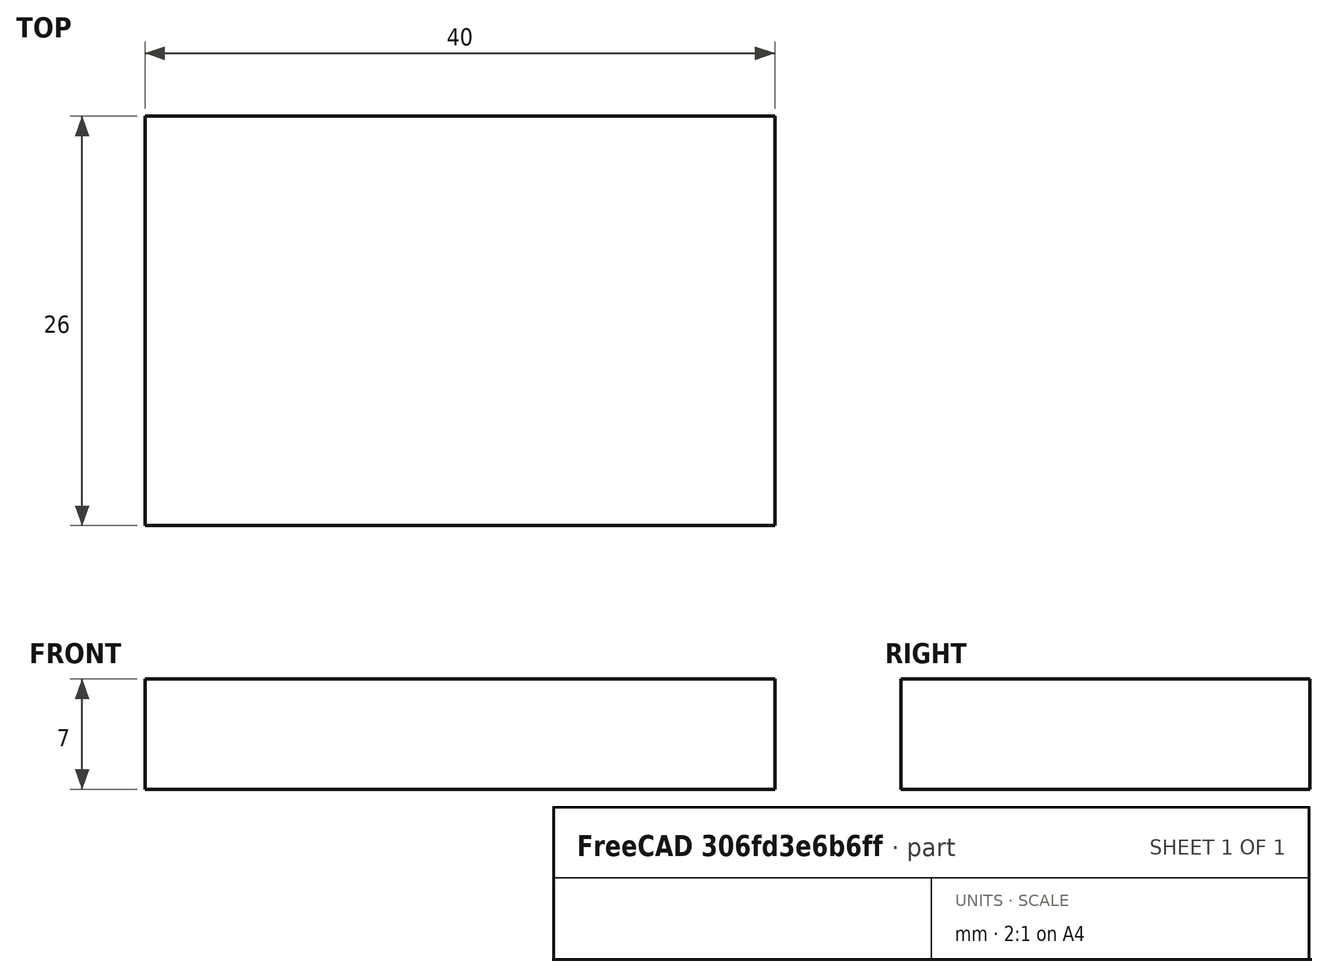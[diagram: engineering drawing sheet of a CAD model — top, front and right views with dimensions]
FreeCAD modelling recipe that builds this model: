
FCSTD DOCUMENT  (FreeCAD 0.17RUnknown)
Label: cam_tail_fix
License: All rights reserved
LicenseURL: http://en.wikipedia.org/wiki/All_rights_reserved
objects: Path::FeaturePython×3, Part::FeaturePython×3, App::FeaturePython×1, Path::FeatureCompoundPython×1
note: 4 computed .brp shape members not serialized (recipe doc carries the construction recipe); baked Part::Feature solids carry a one-line shape summary decoded from their .brp

FEATURE [Path::FeaturePython] Default_Tool  label="Default Tool"  # Path/CAM operation (typed FeaturePython)
  HorizFeed = 3.33333
  HorizRapid = 0
  SpindleDir = 0
  SpindleSpeed = 12000
  ToolNumber = 1
  VertFeed = 1.33333
  VertRapid = 0
  expr: Tool.Diameter = 2
  expr: VertFeed = 80mm / min
  expr: HorizFeed = 200mm / min
  expr: HorizRapid = SetupSheet.HorizRapid
  expr: VertRapid = SetupSheet.VertRapid
FEATURE [App::FeaturePython] SetupSheet  # Path/CAM operation (typed FeaturePython)
  ClearanceHeightExpression = StartDepth+SetupSheet.ClearanceHeightOffset
  ClearanceHeightOffset = 2
  FinalDepthExpression = OpFinalDepth
  HorizRapid = 0
  SafeHeightExpression = StartDepth+SetupSheet.SafeHeightOffset
  SafeHeightOffset = 2
  StartDepthExpression = OpStartDepth
  StepDownExpression = OpToolDiameter
  VertRapid = 0
FEATURE [Part::FeaturePython] tail_01  # a2plus imported part (geometry in sourceFile) (typed FeaturePython)
  fixedPosition = true
  sourceFile = <userpath>/hs/fly/cad/tail.fcstd
  timeLastImport = 1.53696e+09
  updateColors = true
FEATURE [Part::FeaturePython] Clone  label="Base-arm_01"  # Draft clone (typed FeaturePython)
  AttacherType = Attacher::AttachEngine3D
  Fuse = false
  Objects = -> [tail_01]
  PathResource = Base
  Placement = pos=(21,17,-2.5) rot=(-1,0,0;1.5708rad)
  Scale = (1,1,1)
FEATURE [Part::FeaturePython] Stock  # WARN: FeaturePython — macro-defined, semantics opaque (R4)
  Base = -> tail_01
  ExtXneg = 1
  ExtXpos = 1
  ExtYneg = 1
  ExtYpos = 1
  ExtZneg = 1
  ExtZpos = 1
  Placement = pos=(21,17,-3.5) rot=(-1,0,0;1.5708rad)
  StockType = FromBase
FEATURE [Path::FeaturePython] Pocket_Shape002  # Path/CAM operation (typed FeaturePython)
  Active = true
  AreaParams:
    OpenMode = 0
    Angle = 45.0
    MinArcPoints = 4
    Coplanar = 0
    Tolerance = 1e-07
    CleanDistance = 0.0
    PocketExtraOffset = 0.0
    RoundPrecision = 0.0
    AngleShift = 0.0
    SubjectFill = 0
    PocketMode = 2
    Simplify = False
    SectionTolerance = 1e-06
    MaxArcPoints = 100
    Offset = 0.0
    Accuracy = 0.01
    PocketStepover = 2.0
    ClipFill = 0
    ToolRadius = 1.0
    Outline = False
    ClipperScale = 10000000.0
    FromCenter = True
    Explode = False
    EndType = 0
    Shift = 0.0
    ExtraPass = 0
    Project = False
    JoinType = 0
    Thicken = False
    Stepdown = 1.0
    SectionMode = 2
    MiterLimit = 2.0
    Deflection = 0.01
    Reorient = True
    FitArcs = True
    SectionCount = -1
    SectionOffset = 0.0
    Stepover = 0.0
    Unit = 1.0
    Fill = 0
  Base = -> [Clone]
  ClearanceHeight = -1
  CutMode = 0
  ExtraOffset = 0
  FinalDepth = -5.6
  FinishDepth = 0
  KeepToolDown = false
  MinTravel = false
  OffsetPattern = 1
  OpFinalDepth = -5
  OpStartDepth = 0
  OpToolDiameter = 2
  PathParams = {'resume_height': -1.0, 'feedrate': 3.3333333333333335, 'verbose': True, 'orientation': 1, 'return_end': True, 'preamble': False, 'retraction': -1.0, 'feedrate_v': 1.3333333333333333}
  SafeHeight = -1
  StartAt = 0
  StartDepth = -3
  StartPoint = (0,0,0)
  StepDown = 0.1
  StepOver = 100
  ToolController = -> Default_Tool
  UseStartPoint = false
  ZigZagAngle = 45
  expr: ClearanceHeight = StartDepth + SetupSheet.ClearanceHeightOffset
  expr: SafeHeight = StartDepth + SetupSheet.SafeHeightOffset
  expr: StepDown = 0.10000000000000001
  expr: FinalDepth = -5.5999999999999996
  expr: StartDepth = -3
FEATURE [Path::FeatureCompoundPython] Operations  # Path/CAM operation (typed FeaturePython)
  Group = -> [Pocket_Shape002]
  UsePlacements = false
FEATURE [Path::FeaturePython] Job  # Path/CAM operation (typed FeaturePython)
  Base = -> Clone
  GeometryTolerance = 0.01
  Operations = -> Operations
  PostProcessor = 5
  PostProcessorOutputFile = <userpath>/hs/fly/cad/gcode/arm
  SetupSheet = -> SetupSheet
  Stock = -> Stock
  ToolController = -> [Default_Tool]
